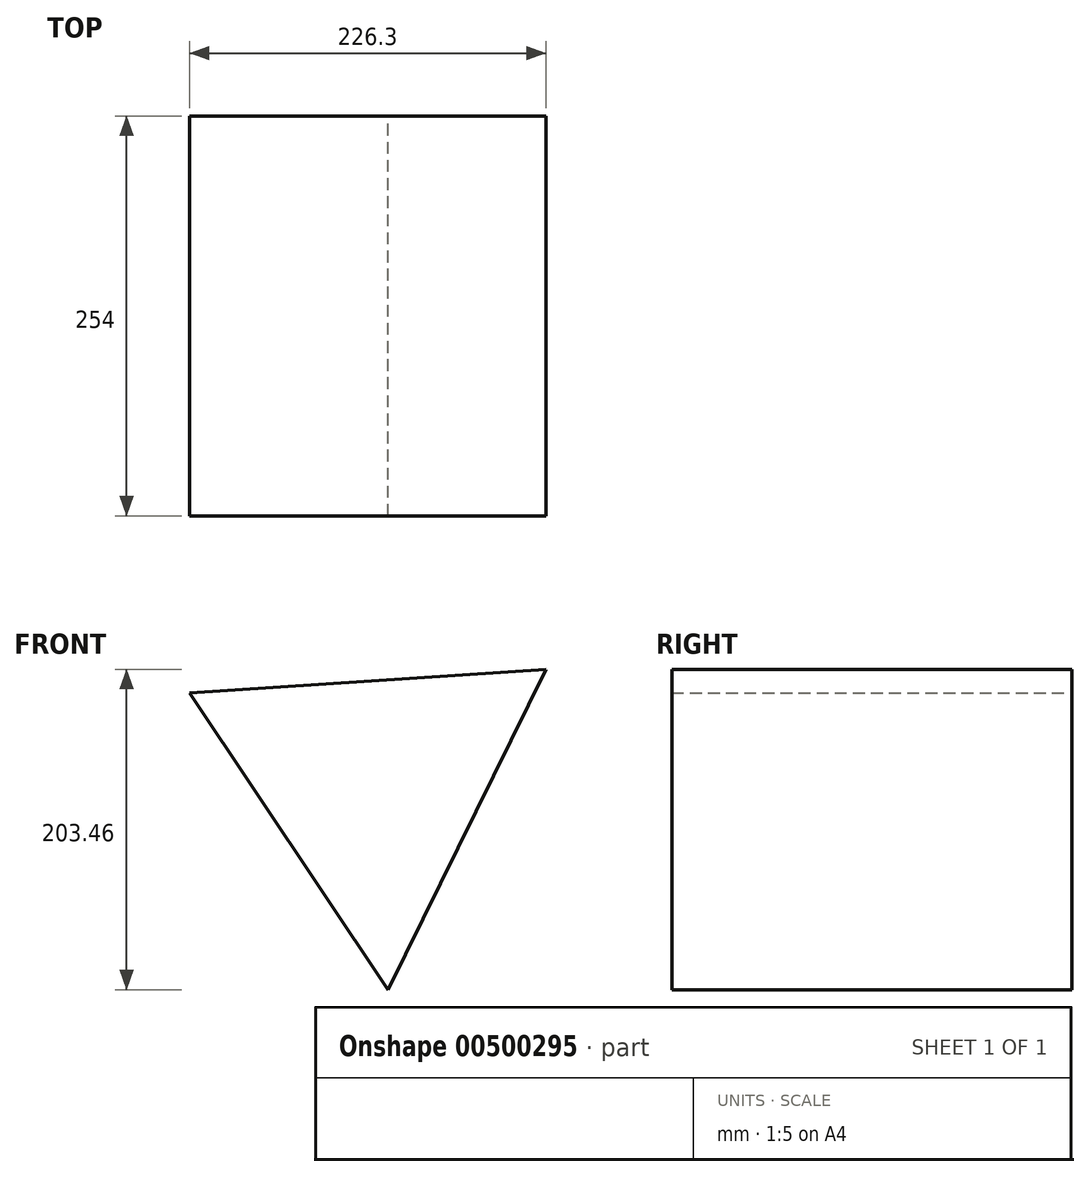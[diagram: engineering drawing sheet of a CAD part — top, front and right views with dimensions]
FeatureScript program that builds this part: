
annotation { "Feature Type Name" : "Feature", "Feature Type Description" : "" }
export const myFeature = defineFeature(function(context is Context, id is Id, definition is map)
    precondition{}
    {
        {
            var Q0;
            Q0=qCreatedBy(makeId("Front.planeOp"),FACE);
            var sketch = newSketch(context, id + "F0", { "sketchPlane" : qUnion([Q0])});
            skCircle(sketch, "E0.cCircle", {"center": v(0, 0) * mm, "radius": 130.94 * mm, "construction": true});
            skLineSegment(sketch, "E0.0", {"start": v(-117.46, 57.86) * mm, "end": v(108.84, 72.8) * mm});
            skLineSegment(sketch, "E0.1", {"start": v(108.84, 72.8) * mm, "end": v(8.63, -130.66) * mm});
            skLineSegment(sketch, "E0.2", {"start": v(8.63, -130.66) * mm, "end": v(-117.46, 57.86) * mm});
            skCircle(sketch, "E1.cCircle", {"center": v(0, 0) * mm, "radius": 61 * mm, "construction": true});
            skLineSegment(sketch, "E1.0", {"start": v(-54.44, 27.53) * mm, "end": v(51.06, 33.38) * mm});
            skLineSegment(sketch, "E1.1", {"start": v(51.06, 33.38) * mm, "end": v(3.38, -60.9) * mm});
            skLineSegment(sketch, "E1.2", {"start": v(3.38, -60.9) * mm, "end": v(-54.44, 27.53) * mm});
            skSolve(sketch);
        }
        {
            var Q0;
            Q0=makeQuery(id+"F0.imprint","IMPRINT",FACE,{"disambiguationData":[TD([[makeQuery(id+"F0.imprint","IMPRINT",EDGE,{"derivedFrom":sQuery(id+"F0.wireOp",EDGE,"E0.0")}),-1.0]])]});
            var Q1;
            Q1=makeQuery(id+"F0.imprint","IMPRINT",FACE,{"disambiguationData":[TD([[makeQuery(id+"F0.imprint","IMPRINT",EDGE,{"derivedFrom":sQuery(id+"F0.wireOp",EDGE,"E1.0")}),-1.0]])]});
            extrude(context, id + "F1", {"entities" : qUnion([Q0, Q1]), "endBound" : BoundingType.SYMMETRIC, "depth" : 254 * mm});
        }
    });
